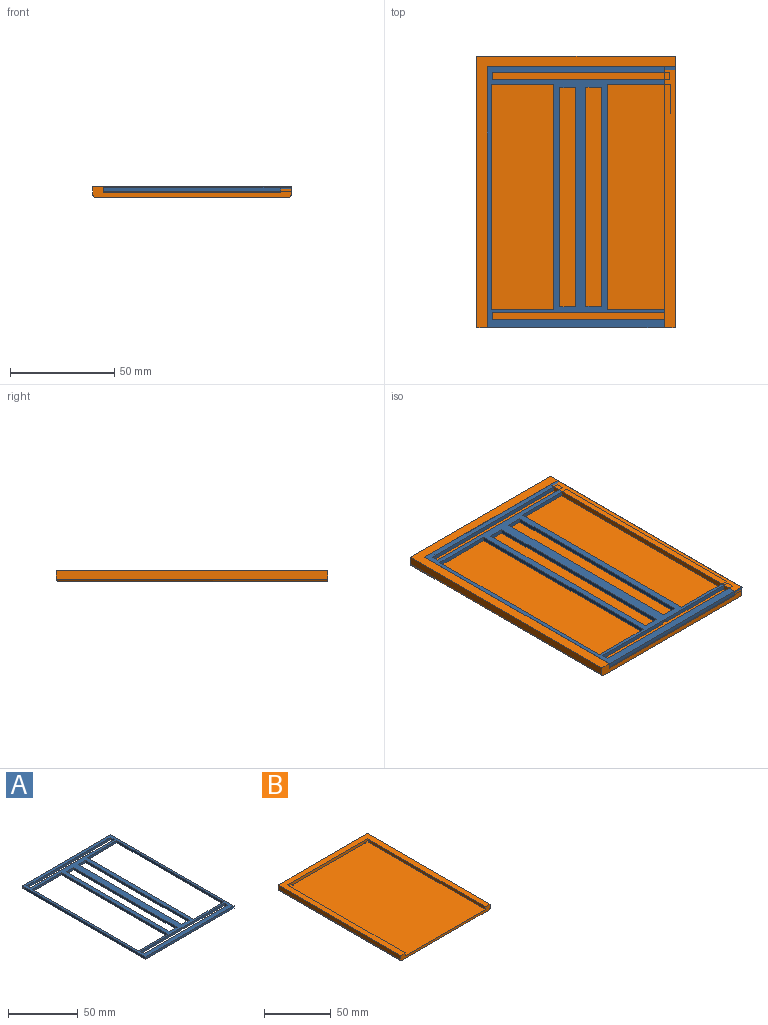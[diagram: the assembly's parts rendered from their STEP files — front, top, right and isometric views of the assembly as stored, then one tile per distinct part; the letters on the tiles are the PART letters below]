
ASSEMBLY  parts=2 mates=1
PART A: 35 faces, bbox 90x125x2 mm
  f0: plane 7.5x2mm, normal (0,-1,0), area 15mm2, adj f1,f27,f28,f29
  f1: plane 105x2mm, normal (-1,0,0), area 210mm2, adj f0,f2,f28,f29
  f2: plane 7.5x2mm, normal (0,1,0), area 15mm2, adj f1,f27,f28,f29
  f3: plane 7.5x2mm, normal (0,-1,0), area 15mm2, adj f4,f21,f28,f29
  f4: plane 105x2mm, normal (-1,0,0), area 210mm2, adj f3,f5,f28,f29
  f5: plane 7.5x2mm, normal (0,1,0), area 15mm2, adj f4,f21,f28,f29
  f6: plane 85x2mm, normal (0,1,0), area 170mm2, adj f7,f22,f28,f29
  f7: plane 3.5x2mm, normal (1,0,0), area 7mm2, adj f6,f8,f28,f29
  f8: plane 85x2mm, normal (0,-1,0), area 167.6mm2, adj f7,f22,f28,f29,f34
  f9: plane 30.25x2mm, normal (0,-1,0), area 60.5mm2, adj f10,f23,f28,f29
  f10: plane 108x2mm, normal (-1,0,0), area 216mm2, adj f9,f11,f28,f29
  f11: plane 30.25x2mm, normal (0,1,0), area 60.5mm2, adj f10,f23,f28,f29
  f12: plane 29.75x2mm, normal (0,-1,0), area 59.5mm2, adj f13,f24,f28,f29
  f13: plane 108x2mm, normal (-1,0,0), area 216mm2, adj f12,f14,f28,f29
  f14: plane 29.75x2mm, normal (0,1,0), area 59.5mm2, adj f13,f24,f28,f29
  f15: plane 3.5x2mm, normal (1,0,0), area 7mm2, adj f16,f25,f28,f29
  f16: plane 85x2mm, normal (0,-1,0), area 170mm2, adj f15,f17,f28,f29
  f17: plane 3.5x2mm, normal (-1,0,0), area 7mm2, adj f16,f25,f28,f29
  f18: plane 125x2mm, normal (1,0,0), area 248.9mm2, adj f19,f26,f28,f29,f32
  f19: plane 90x2mm, normal (0,1,0), area 180mm2, adj f18,f20,f28,f29
  f20: plane 125x2mm, normal (-1,0,0), area 248.9mm2, adj f19,f26,f28,f29,f30
  f21: plane 105x2mm, normal (1,0,0), area 210mm2, adj f3,f5,f28,f29
  f22: plane 3.5x2mm, normal (-1,0,0), area 7mm2, adj f6,f8,f28,f29
  f23: plane 108x2mm, normal (1,0,0), area 216mm2, adj f9,f11,f28,f29
  f24: plane 108x2mm, normal (1,0,0), area 216mm2, adj f12,f14,f28,f29
  f25: plane 85x2mm, normal (0,1,0), area 167.6mm2, adj f15,f17,f28,f29,f34
  f26: plane 90x2mm, normal (0,-1,0), area 180mm2, adj f18,f20,f28,f29
  f27: plane 105x2mm, normal (1,0,0), area 210mm2, adj f0,f2,f28,f29
  f28: plane 125x90mm, normal (0,0,1), area 2600mm2, adj f0,f1,f2,f3,f4,f5,f6,f7
  f29: plane 125x90mm, normal (0,0,-1), area 2275.3mm2, adj f0,f1,f2,f3,f4,f5,f6,f7
  f30: cylinder r=0.6mm len=5mm, axis (-1,0,0), area 18.8mm2, adj f20,f31
  f31: plane 1.2x1.2mm, normal (-1,0,0), area 1.1mm2, adj f30
  f32: cylinder r=0.6mm len=5mm, axis (1,0,0), area 18.8mm2, adj f18,f33
  f33: plane 1.2x1.2mm, normal (1,0,0), area 1.1mm2, adj f32
  f34: cylinder r=1.5mm len=111.77mm, axis (0,1,0), area 442.2mm2, adj f8,f25,f29
PART B: 17 faces, bbox 95x130x5 mm
  f0: plane 95x5mm, normal (0,-1,0), area 253.6mm2, adj f1,f2,f4,f5,f6,f8,f9,f14
  f1: plane 130x95mm, normal (0,0,1), area 1725mm2, adj f0,f2,f3,f4,f6,f7,f8
  f2: plane 130x4mm, normal (1,0,0), area 520mm2, adj f0,f1,f3,f14
  f3: plane 95x4mm, normal (0,1,0), area 380mm2, adj f1,f2,f4,f16
  f4: plane 130x4mm, normal (-1,0,0), area 520mm2, adj f0,f1,f3,f15
  f5: plane 129x93mm, normal (0,0,-1), area 11997mm2, adj f0,f14,f15,f16
  f6: plane 125x2.6mm, normal (-1,0,0), area 324.2mm2, adj f0,f1,f7,f9,f12
  f7: plane 85x2.6mm, normal (0,-1,0), area 221mm2, adj f1,f6,f8,f9
  f8: plane 125x2.6mm, normal (1,0,0), area 324.2mm2, adj f0,f1,f7,f9,f10
  f9: plane 125x85mm, normal (0,0,1), area 10625mm2, adj f0,f6,f7,f8
  f10: cylinder r=0.5mm len=4mm, axis (-1,0,0), area 12.6mm2, adj f8,f11
  f11: plane 1x1mm, normal (1,0,0), area 0.8mm2, adj f10
  f12: cylinder r=0.5mm len=4mm, axis (1,0,0), area 12.6mm2, adj f6,f13
  f13: plane 1x1mm, normal (-1,0,0), area 0.8mm2, adj f12
  f14: cylinder r=1mm len=130mm, axis (0,1,0), area 203.6mm2, adj f0,f2,f5,f16
  f15: cylinder r=1mm len=130mm, axis (0,-1,0), area 203.6mm2, adj f0,f4,f5,f16
  f16: cylinder r=1mm len=95mm, axis (-1,0,0), area 148.1mm2, adj f3,f5,f14,f15
PLACE A rot(axis=(1,0,0),0.1deg) t=(-34.55,60,1.94)mm
PLACE B t=(-47.5,65,-1)mm
MATE revolute B.f12 <-> A.f32  axis (1,0,0) through (-90,123.5,3)mm
